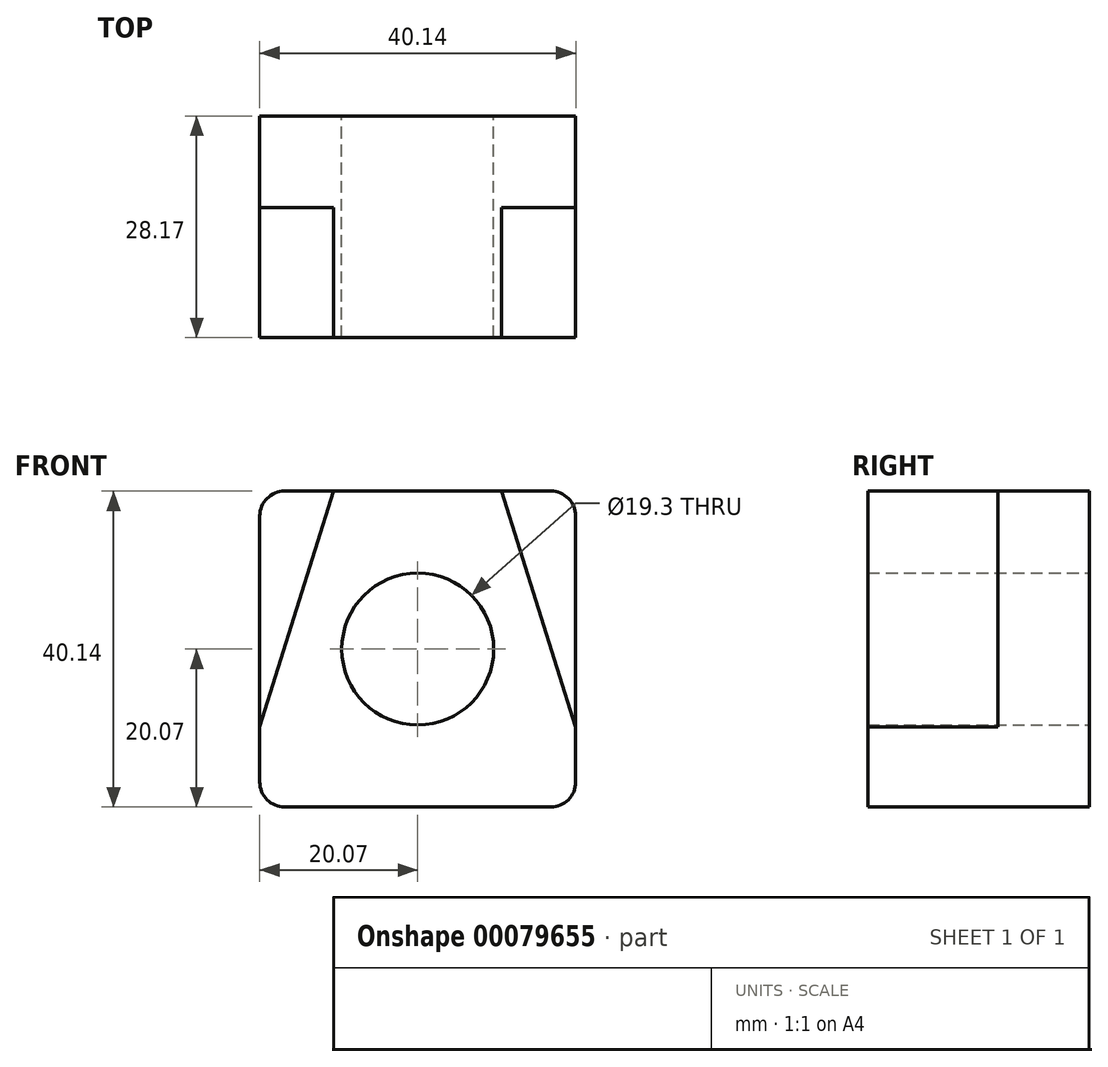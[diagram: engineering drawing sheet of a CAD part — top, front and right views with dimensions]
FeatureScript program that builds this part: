
annotation { "Feature Type Name" : "Feature", "Feature Type Description" : "" }
export const myFeature = defineFeature(function(context is Context, id is Id, definition is map)
    precondition{}
    {
        {
            var Q0;
            Q0=qCreatedBy(makeId("Front.planeOp"),FACE);
            var sketch = newSketch(context, id + "F0", { "sketchPlane" : qUnion([Q0])});
            skLineSegment(sketch, "E0.bottom", {"start": v(20.07, 20.07) * mm, "end": v(-20.07, 20.07) * mm});
            skLineSegment(sketch, "E0.top", {"start": v(20.07, -20.07) * mm, "end": v(-20.07, -20.07) * mm});
            skLineSegment(sketch, "E0.left", {"start": v(20.07, 20.07) * mm, "end": v(20.07, -20.07) * mm});
            skLineSegment(sketch, "E0.right", {"start": v(-20.07, 20.07) * mm, "end": v(-20.07, -20.07) * mm});
            skPoint(sketch, "E0.middle", {"position": v(0, 0) * mm});
            skSolve(sketch);
        }
        {
            var Q0;
            Q0 = qSketchRegion(id + "F0", true);
            extrude(context, id + "F1", {"entities" : qUnion([Q0]), "depth" : 11.66 * mm});
        }
        {
            var Q0;
            Q0=makeQuery(id+"F1.opExtrude","CAP_FACE",FACE,{"disambiguationData":[OSD([sQuery(id+"F0.wireOp",EDGE,"E0.bottom"),sQuery(id+"F0.wireOp",EDGE,"E0.top"),sQuery(id+"F0.wireOp",EDGE,"E0.left"),sQuery(id+"F0.wireOp",EDGE,"E0.right")])],"isStart":false});
            var sketch = newSketch(context, id + "F2", { "sketchPlane" : qUnion([Q0])});
            skLineSegment(sketch, "E1", {"start": v(-20.07, -20.07) * mm, "end": v(-20.07, -9.92) * mm});
            skLineSegment(sketch, "E2", {"start": v(-20.07, -20.07) * mm, "end": v(20.07, -20.07) * mm});
            skLineSegment(sketch, "E3", {"start": v(20.07, -20.07) * mm, "end": v(20.07, -9.92) * mm});
            skLineSegment(sketch, "E4", {"start": v(20.07, -9.92) * mm, "end": v(10.67, 20.07) * mm});
            skLineSegment(sketch, "E5", {"start": v(10.67, 20.07) * mm, "end": v(-10.67, 20.07) * mm});
            skLineSegment(sketch, "E6", {"start": v(-10.67, 20.07) * mm, "end": v(-20.07, -9.92) * mm});
            skLineSegment(sketch, "E7", {"start": v(-10.67, 20.07) * mm, "end": v(10.67, 20.07) * mm});
            skSolve(sketch);
        }
        {
            var Q0;
            Q0=makeQuery(id+"F2.imprint","IMPRINT",FACE,{"disambiguationData":[TD([[makeQuery(id+"F2.imprint","IMPRINT",EDGE,{"derivedFrom":sQuery(id+"F2.wireOp",EDGE,"E1")}),1.0]])]});
            extrude(context, id + "F3", {"entities" : qUnion([Q0]), "operationType" : NewBodyOperationType.ADD, "depth" : 16.5 * mm});
        }
        {
            var Q0;
            Q0=makeQuery(id+"F1.opExtrude","CAP_FACE",FACE,{"disambiguationData":[OSD([sQuery(id+"F0.wireOp",EDGE,"E0.bottom"),sQuery(id+"F0.wireOp",EDGE,"E0.top"),sQuery(id+"F0.wireOp",EDGE,"E0.left"),sQuery(id+"F0.wireOp",EDGE,"E0.right")])],"isStart":true});
            var sketch = newSketch(context, id + "F4", { "sketchPlane" : qUnion([Q0])});
            skCircle(sketch, "E8", {"center": v(0, 0) * mm, "radius": 9.65 * mm});
            skSolve(sketch);
        }
        {
            var Q0;
            Q0 = qSketchRegion(id + "F4", true);
            extrude(context, id + "F5", {"entities" : qUnion([Q0]), "operationType" : NewBodyOperationType.REMOVE, "oppositeDirection" : true, "depth" : 30.48 * mm});
        }
        {
            var Q0;
            Q0=makeQuery(id+"F1.opExtrude","SWEPT_EDGE",EDGE,{"disambiguationData":[OSD([sQuery(id+"F0.wireOp",EDGE,"E0.bottom"),sQuery(id+"F0.wireOp",EDGE,"E0.right")])]});
            fillet(context, id + "F6", {"entities" : qUnion([Q0]), "radius" : 3.17 * mm, "tangentPropagation" : true, "allowEdgeOverflow" : false});
        }
        {
            var Q0;
            Q0=makeQuery(id+"F3.boolean.opBoolean","MERGE",EDGE,{"derivedFrom":[makeQuery(id+"F1.opExtrude","SWEPT_EDGE",EDGE,{"disambiguationData":[OSD([sQuery(id+"F0.wireOp",EDGE,"E0.top"),sQuery(id+"F0.wireOp",EDGE,"E0.right")])]}),makeQuery(id+"F3.opExtrude","SWEPT_EDGE",EDGE,{"disambiguationData":[OSD([sQuery(id+"F2.wireOp",EDGE,"E1"),sQuery(id+"F2.wireOp",EDGE,"E2")])]})]});
            fillet(context, id + "F7", {"entities" : qUnion([Q0]), "radius" : 3.17 * mm, "tangentPropagation" : true, "allowEdgeOverflow" : false});
        }
        {
            var Q0;
            Q0=makeQuery(id+"F1.opExtrude","SWEPT_EDGE",EDGE,{"disambiguationData":[OSD([sQuery(id+"F0.wireOp",EDGE,"E0.bottom"),sQuery(id+"F0.wireOp",EDGE,"E0.left")])]});
            var Q1;
            Q1=makeQuery(id+"F3.boolean.opBoolean","MERGE",EDGE,{"derivedFrom":[makeQuery(id+"F1.opExtrude","SWEPT_EDGE",EDGE,{"disambiguationData":[OSD([sQuery(id+"F0.wireOp",EDGE,"E0.top"),sQuery(id+"F0.wireOp",EDGE,"E0.left")])]}),makeQuery(id+"F3.opExtrude","SWEPT_EDGE",EDGE,{"disambiguationData":[OSD([sQuery(id+"F2.wireOp",EDGE,"E2"),sQuery(id+"F2.wireOp",EDGE,"E3")])]})]});
            fillet(context, id + "F8", {"entities" : qUnion([Q0, Q1]), "radius" : 3.17 * mm, "tangentPropagation" : true, "allowEdgeOverflow" : false});
        }
    });
